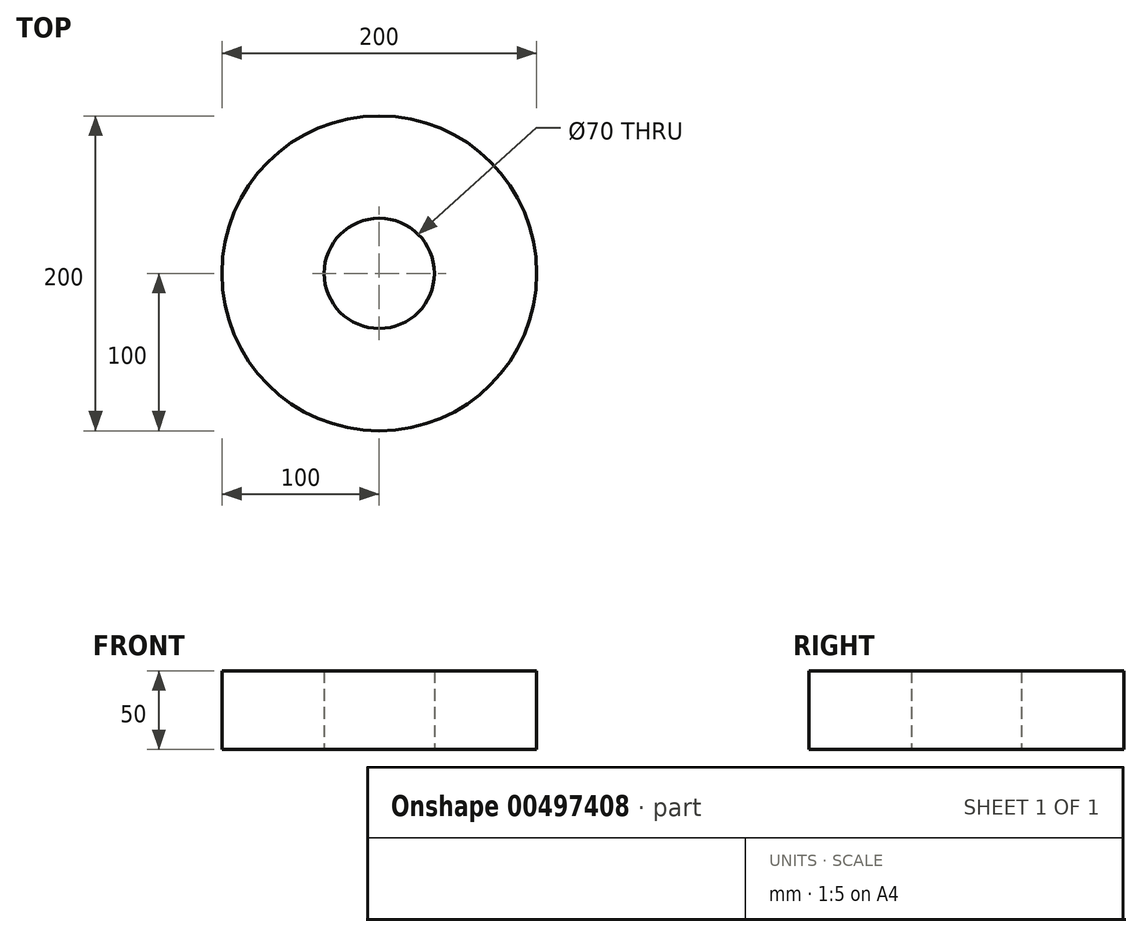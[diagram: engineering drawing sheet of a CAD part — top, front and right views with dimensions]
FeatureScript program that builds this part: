
annotation { "Feature Type Name" : "Feature", "Feature Type Description" : "" }
export const myFeature = defineFeature(function(context is Context, id is Id, definition is map)
    precondition{}
    {
        {
            var Q0;
            Q0=qCreatedBy(makeId("Top.planeOp"),FACE);
            var sketch = newSketch(context, id + "F0", { "sketchPlane" : qUnion([Q0])});
            skCircle(sketch, "E0", {"center": v(0, 0) * mm, "radius": 100 * mm});
            skCircle(sketch, "E1", {"center": v(0, 0) * mm, "radius": 35 * mm});
            skSolve(sketch);
        }
        {
            var Q0;
            Q0=makeQuery(id+"F0.imprint","IMPRINT",FACE,{"disambiguationData":[TD([[makeQuery(id+"F0.imprint","IMPRINT",EDGE,{"derivedFrom":sQuery(id+"F0.wireOp",EDGE,"E0")}),1.0]])]});
            extrude(context, id + "F1", {"entities" : qUnion([Q0]), "depth" : 50 * mm});
        }
    });
